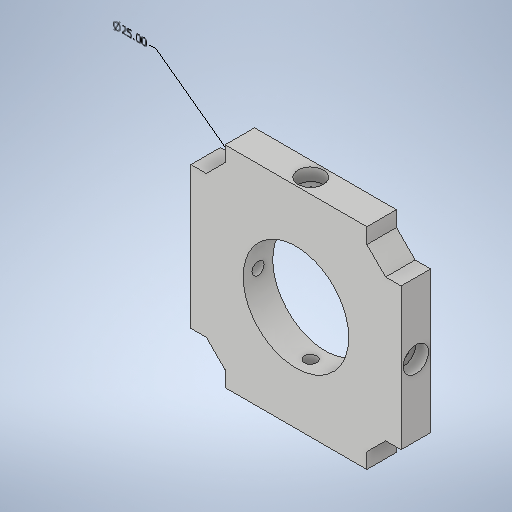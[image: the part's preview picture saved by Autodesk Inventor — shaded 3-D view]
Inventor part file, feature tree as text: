
AUTODESK INVENTOR PART (.ipt)
format: ipt  version: 2025.1 (Build 291241000, 241)  size: 300,032 bytes
history: native  units: mm
features: sketch x6, hole x5, extrude x1, other x1
ambient origin geometry x8: Origin, YZ Plane, XZ Plane, XY Plane, X Axis, Y Axis, Z Axis, Center Point
bodies: 实体1 (feature_tree)
feature tree (13):
  extrude  "拉伸1"  Depth=3.0mm
  hole  "孔1"  [1 undecoded]
  hole  "孔2"  [1 undecoded]
  hole  "孔3"  [1 undecoded]
  hole  "孔4"  [1 undecoded]
  hole  "孔5"  [1 undecoded]
  sketch  "草图1"  dims[d18=7.0mm d19=0.0mm]
  sketch  "草图2"  dims[d20=2.9mm d21=6.0mm d22=6.0mm d23=3.0mm d24=90.0deg d25=8.0mm d26=20.594885mm]
  sketch  "草图3"  dims[d27=2.9mm d28=6.0mm d29=6.0mm d30=3.0mm d31=90.0deg d32=8.0mm d33=20.594885mm]
  sketch  "草图4"  dims[d34=2.9mm d35=6.0mm d36=6.0mm d37=3.0mm d38=90.0deg d39=8.0mm d40=20.594885mm]
  sketch  "草图5"  dims[d41=2.9mm d42=6.0mm d43=6.0mm d44=3.0mm d45=90.0deg d46=8.0mm d47=20.594885mm]
  sketch  "草图6"  dims[d48=25.0mm d49=6.0mm d50=6.0mm d51=3.0mm d52=90.0deg d53=0.5mm d54=20.594885mm d55=6.326251mm d56=25.0mm]
  other  "直径尺寸 1"
note: 5 required parameter values undecoded (feature->parameter linkage not recoverable at this tier; creation-order binding heuristic only, values carry confidence <= 0.55)
